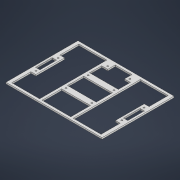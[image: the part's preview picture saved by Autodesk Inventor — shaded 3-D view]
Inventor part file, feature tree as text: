
AUTODESK INVENTOR PART (.ipt)
format: ipt  version: 2021 (Build 250183000, 183)  size: 419,840 bytes
history: native  units: mm
features: extrude x7, sketch x3
ambient origin geometry x8: Origin, YZ Plane, XZ Plane, XY Plane, X Axis, Y Axis, Z Axis, Center Point
bodies: Volumenkörper1 (feature_tree)
feature tree (10):
  extrude  "Extrusion1"  Depth=150.0mm
  sketch  "Skizze11"  dims[d2=3.0mm d3=0.0mm d50=3.2mm]
  extrude  "Extrusion12"  Depth=3.0mm
  extrude  "Extrusion13"  Depth=4.0mm
  extrude  "Extrusion14"  Depth=4.0mm
  extrude  "Extrusion15"  Depth=4.0mm
  extrude  "Extrusion16"  Depth=4.0mm
  extrude  "Extrusion17"  Depth=4.0mm TaperAngle=0.0deg
  sketch  "Skizze1"  dims[d0=200.0mm d1=150.0mm]
  sketch  "Skizze12"  dims[d51=3.2mm d52=23.0mm d53=23.0mm d54=73.0mm d55=73.0mm d56=17.5mm d57=0.0mm d60=10.0mm d61=0.0mm d62=3.2mm d63=3.2mm d64=27.0mm d65=27.0mm d66=52.0mm d67=52.0mm d68=10.0mm d69=0.0mm d70=3.2mm d71=3.2mm d72=23.0mm d73=23.0mm d74=10.5mm d75=10.5mm d76=3.2mm d77=3.2mm d78=10.5mm d79=10.5mm d80=23.0mm d81=23.0mm d82=10.0mm d83=0.0mm d84=3.2mm d85=3.2mm d86=23.0mm d87=23.0mm d88=15.0mm d89=15.0mm d90=10.0mm d91=0.0mm d92=10.0mm d93=0.0mm d94=5.0mm d95=7.0mm d96=5.0mm d97=65.0mm d98=7.0mm d99=65.0mm d100=40.0mm d101=25.0mm d102=21.0mm d103=5.0mm d104=5.0mm d105=5.0mm d106=5.0mm d107=10.0mm d108=60.0mm d109=17.0mm d110=7.0mm d111=10.0mm d112=60.0mm d113=17.0mm d114=7.0mm d115=5.0mm d116=12.0mm d117=17.0mm d118=12.0mm d119=5.0mm d120=5.0mm d121=4.0mm d122=4.0mm d123=4.0mm d124=4.0mm d126=5.6mm d127=4.0mm d128=4.0mm d129=4.0mm d130=4.0mm d131=4.0mm]
